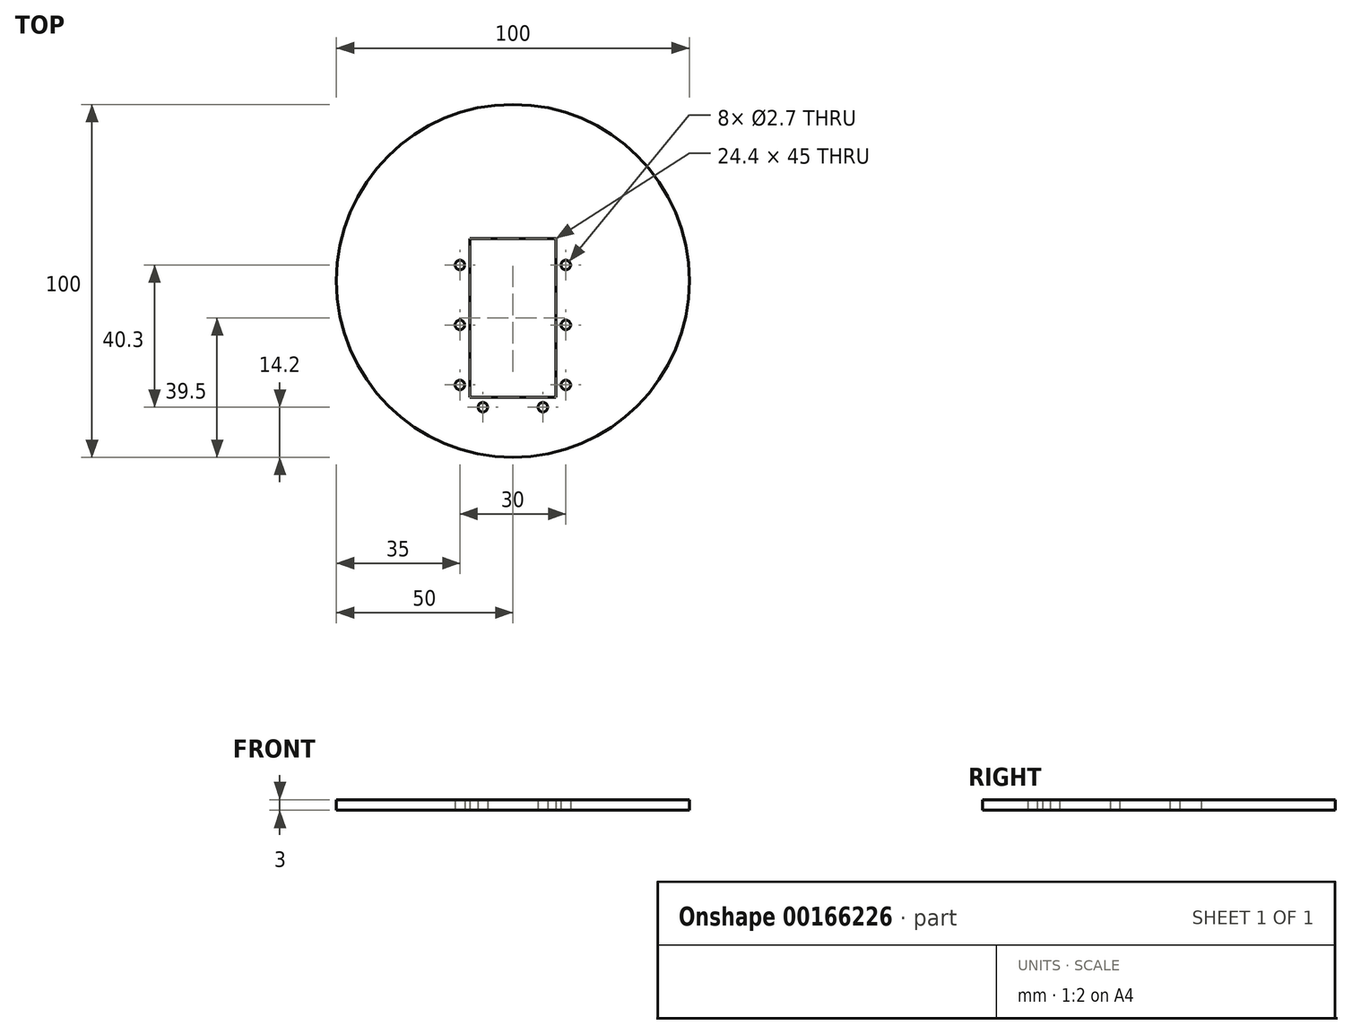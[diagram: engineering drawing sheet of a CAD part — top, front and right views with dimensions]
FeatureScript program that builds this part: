
annotation { "Feature Type Name" : "Feature", "Feature Type Description" : "" }
export const myFeature = defineFeature(function(context is Context, id is Id, definition is map)
    precondition{}
    {
        {
            var Q0;
            Q0=qCreatedBy(makeId("Top.planeOp"),FACE);
            var sketch = newSketch(context, id + "F0", { "sketchPlane" : qUnion([Q0])});
            skLineSegment(sketch, "E0.bottom", {"start": v(-12.2, 12) * mm, "end": v(12.2, 12) * mm});
            skLineSegment(sketch, "E0.top", {"start": v(-12.2, -33) * mm, "end": v(12.2, -33) * mm});
            skLineSegment(sketch, "E0.left", {"start": v(-12.2, 12) * mm, "end": v(-12.2, -33) * mm});
            skLineSegment(sketch, "E0.right", {"start": v(12.2, 12) * mm, "end": v(12.2, -33) * mm});
            skCircle(sketch, "E1", {"center": v(-15, 4.5) * mm, "radius": 1.35 * mm});
            skCircle(sketch, "E2.0.1.0", {"center": v(-15, -12.5) * mm, "radius": 1.35 * mm});
            skCircle(sketch, "E2.0.2.0", {"center": v(-15, -29.5) * mm, "radius": 1.35 * mm});
            skCircle(sketch, "E2.1.0.0", {"center": v(15, 4.5) * mm, "radius": 1.35 * mm});
            skCircle(sketch, "E2.1.1.0", {"center": v(15, -12.5) * mm, "radius": 1.35 * mm});
            skCircle(sketch, "E2.1.2.0", {"center": v(15, -29.5) * mm, "radius": 1.35 * mm});
            skLineSegment(sketch, "E2.direction1", {"start": v(-15, 4.5) * mm, "end": v(15, 4.5) * mm, "construction": true});
            skLineSegment(sketch, "E2.direction2", {"start": v(-15, 4.5) * mm, "end": v(-15, -12.5) * mm, "construction": true});
            skCircle(sketch, "E3", {"center": v(-8.5, -35.8) * mm, "radius": 1.35 * mm});
            skCircle(sketch, "E4.MirrorC", {"center": v(8.5, -35.8) * mm, "radius": 1.35 * mm});
            skSolve(sketch);
        }
        {
            var Q0;
            Q0=qCreatedBy(makeId("Top.planeOp"),FACE);
            var sketch = newSketch(context, id + "F1", { "sketchPlane" : qUnion([Q0])});
            skCircle(sketch, "E5", {"center": v(0, 0) * mm, "radius": 50 * mm});
            skSolve(sketch);
        }
        {
            var Q0;
            Q0=makeQuery(id+"F1.imprint","IMPRINT",FACE,{"disambiguationData":[TD([[makeQuery(id+"F1.imprint","IMPRINT",EDGE,{"derivedFrom":sQuery(id+"F1.wireOp",EDGE,"E5")}),1.0]])]});
            extrude(context, id + "F2", {"entities" : qUnion([Q0]), "depth" : 3 * mm});
        }
        {
            var Q0;
            Q0 = qSketchRegion(id + "F0", true);
            extrude(context, id + "F3", {"entities" : qUnion([Q0]), "operationType" : NewBodyOperationType.REMOVE, "depth" : 25 * mm});
        }
    });
